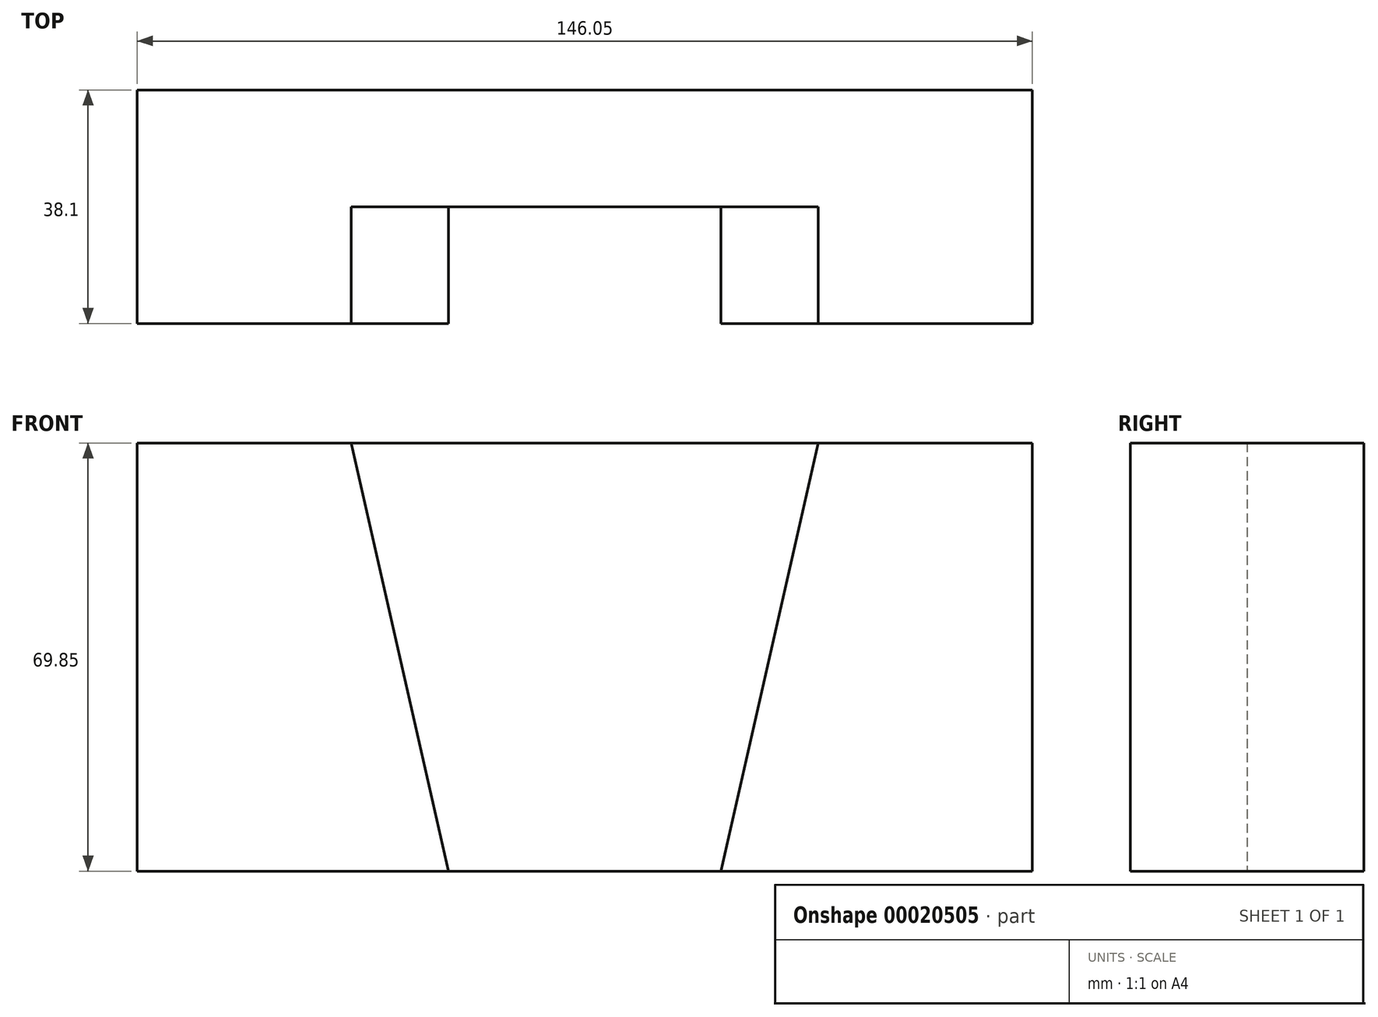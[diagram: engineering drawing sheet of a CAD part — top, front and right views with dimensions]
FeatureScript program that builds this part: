
annotation { "Feature Type Name" : "Feature", "Feature Type Description" : "" }
export const myFeature = defineFeature(function(context is Context, id is Id, definition is map)
    precondition{}
    {
        {
            var Q0;
            Q0=qCreatedBy(makeId("Front.planeOp"),FACE);
            var sketch = newSketch(context, id + "F0", { "sketchPlane" : qUnion([Q0])});
            skLineSegment(sketch, "E0.left", {"start": v(-50.8, 39.59) * mm, "end": v(-50.8, -30.26) * mm});
            skLineSegment(sketch, "E0.right", {"start": v(22.23, 39.59) * mm, "end": v(22.23, -30.26) * mm});
            skLineSegment(sketch, "E1", {"start": v(-50.8, 39.59) * mm, "end": v(-15.87, 39.59) * mm});
            skLineSegment(sketch, "E2", {"start": v(-15.87, 39.59) * mm, "end": v(0, -30.26) * mm});
            skLineSegment(sketch, "E3", {"start": v(-15.87, 39.59) * mm, "end": v(22.23, 39.59) * mm});
            skLineSegment(sketch, "E4", {"start": v(-50.8, -30.26) * mm, "end": v(0, -30.26) * mm});
            skLineSegment(sketch, "E5", {"start": v(-50.8, -30.26) * mm, "end": v(22.23, -30.26) * mm});
            skLineSegment(sketch, "E6", {"start": v(-50.8, -30.26) * mm, "end": v(5.7, -30.26) * mm});
            skSolve(sketch);
        }
        {
            var Q0;
            {var subQ2=sQuery(id+"F0.wireOp",EDGE,"E0.left");Q0=makeQuery(id+"F0.imprint","IMPRINT",FACE,{"disambiguationData":[TD([[makeQuery(id+"F0.imprint","IMPRINT",EDGE,{"derivedFrom":subQ2}),1.0]])]});}
            extrude(context, id + "F1", {"entities" : qUnion([Q0]), "depth" : 38.1 * mm});
        }
        {
            var Q0;
            {var subQ2=sQuery(id+"F0.wireOp",EDGE,"E0.right");Q0=makeQuery(id+"F0.imprint","IMPRINT",FACE,{"disambiguationData":[TD([[makeQuery(id+"F0.imprint","IMPRINT",EDGE,{"derivedFrom":subQ2}),-1.0]])]});}
            extrude(context, id + "F2", {"entities" : qUnion([Q0]), "operationType" : NewBodyOperationType.ADD, "depth" : 19.05 * mm});
        }
        {
            var Q0;
            Q0=makeQuery(id+"F1.opExtrude","SWEPT_BODY",BODY,{"disambiguationData":[OSD([sQuery(id+"F0.wireOp",EDGE,"E0.left"),sQuery(id+"F0.wireOp",EDGE,"E1"),sQuery(id+"F0.wireOp",EDGE,"E2"),sQuery(id+"F0.wireOp",EDGE,"E4")])]});
            var Q1;
            Q1=makeQuery(id+"F2.opExtrude","SWEPT_FACE",FACE,{"disambiguationData":[OSD([sQuery(id+"F0.wireOp",EDGE,"E0.right")])]});
            mirror(context, id + "F3", {"operationType" : NewBodyOperationType.ADD, "entities" : qUnion([Q0]), "mirrorPlane" : qUnion([Q1])});
        }
    });
